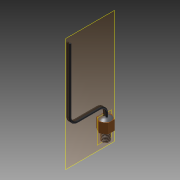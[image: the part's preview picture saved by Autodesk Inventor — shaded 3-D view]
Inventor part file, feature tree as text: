
AUTODESK INVENTOR PART (.ipt)
format: ipt  version: 2015 (Build 190159000, 159)  size: 136,704 bytes
history: native  units: mm
features: extrude x3, chamfer x1, thread x1, revolve x1, plane x1, sweep x1, mirror x1
ambient origin geometry x8: Origin, YZ Plane, XZ Plane, XY Plane, X Axis, Y Axis, Z Axis, Center Point
bodies: Solid1 (feature_tree)
feature tree (9):
  extrude  "Extrusión1"  Depth=4.68mm
  extrude  "Extrusión2"  Depth=4.0mm TaperAngle=0.0deg
  chamfer  "Chaflán1"  Distance=3.0mm
  extrude  "Extrusión3"  Depth=4.0mm TaperAngle=0.0deg
  thread  "Rosca1"  [1 undecoded]
  revolve  "Revolución1"  [1 undecoded]
  plane  "Plano de trabajo1"
  sweep  "Barrido1"
  mirror  "Simetría1"
note: 2 required parameter values undecoded (feature->parameter linkage not recoverable at this tier; creation-order binding heuristic only, values carry confidence <= 0.55)